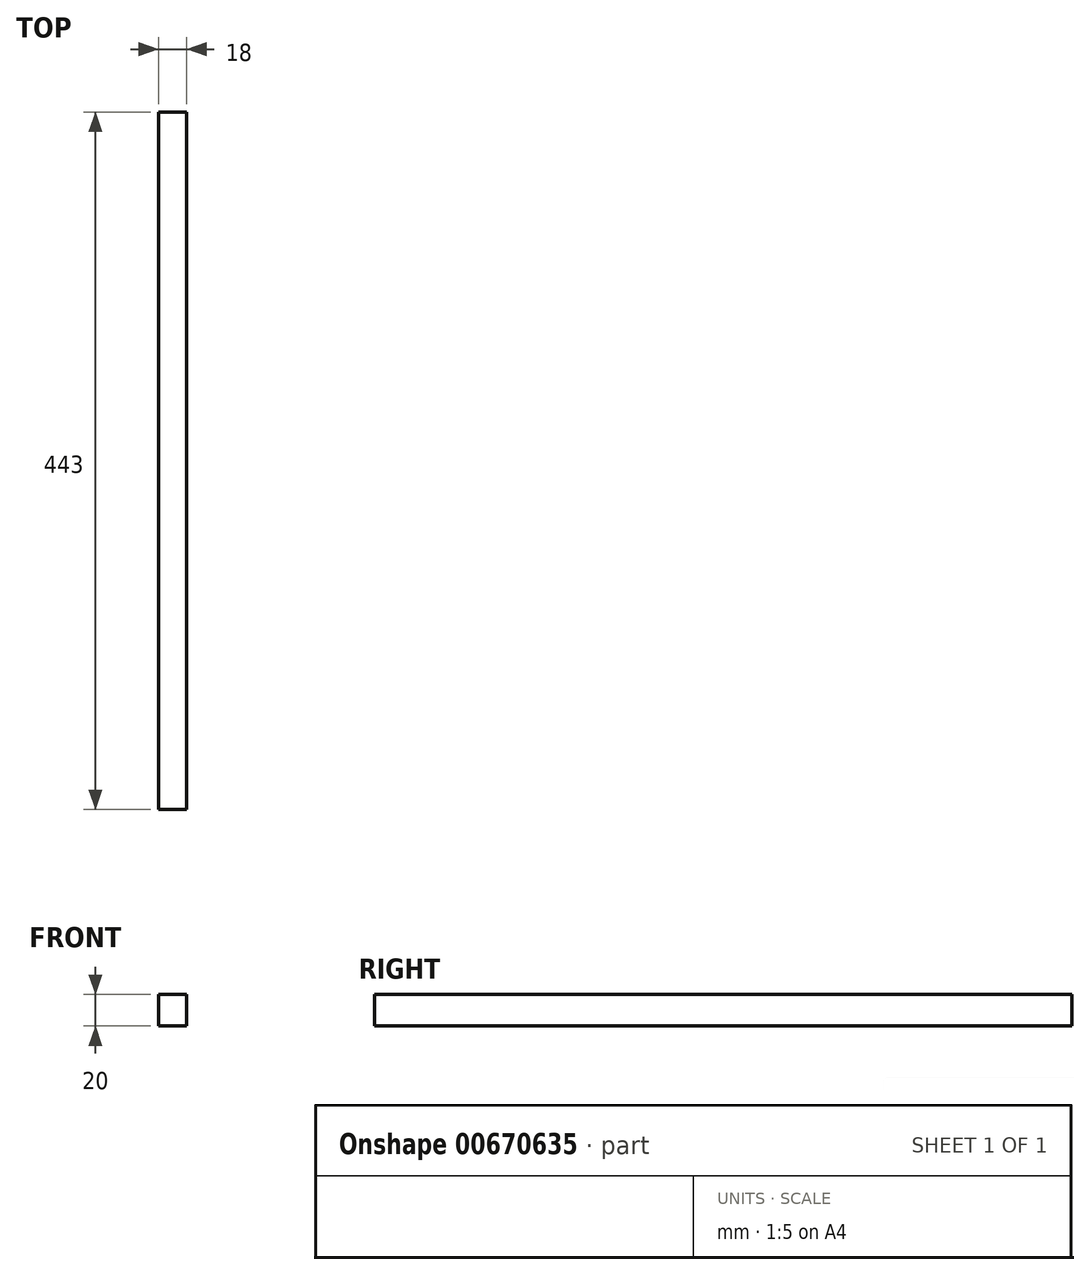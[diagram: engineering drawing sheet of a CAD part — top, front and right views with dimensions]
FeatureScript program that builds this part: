
annotation { "Feature Type Name" : "Feature", "Feature Type Description" : "" }
export const myFeature = defineFeature(function(context is Context, id is Id, definition is map)
    precondition{}
    {
        {
            var Q0;
            Q0=qCreatedBy(makeId("Top.planeOp"),FACE);
            var sketch = newSketch(context, id + "F0", { "sketchPlane" : qUnion([Q0])});
            skLineSegment(sketch, "E0.bottom", {"start": v(9, 221.5) * mm, "end": v(-9, 221.5) * mm});
            skLineSegment(sketch, "E0.top", {"start": v(9, -221.5) * mm, "end": v(-9, -221.5) * mm});
            skLineSegment(sketch, "E0.left", {"start": v(9, 221.5) * mm, "end": v(9, -221.5) * mm});
            skLineSegment(sketch, "E0.right", {"start": v(-9, 221.5) * mm, "end": v(-9, -221.5) * mm});
            skPoint(sketch, "E0.middle", {"position": v(0, 0) * mm});
            skSolve(sketch);
        }
        {
            var Q0;
            Q0 = qSketchRegion(id + "F0", true);
            extrude(context, id + "F1", {"entities" : qUnion([Q0]), "endBound" : BoundingType.SYMMETRIC, "depth" : 20 * mm, "offsetDistance" : 25 * mm});
        }
    });
